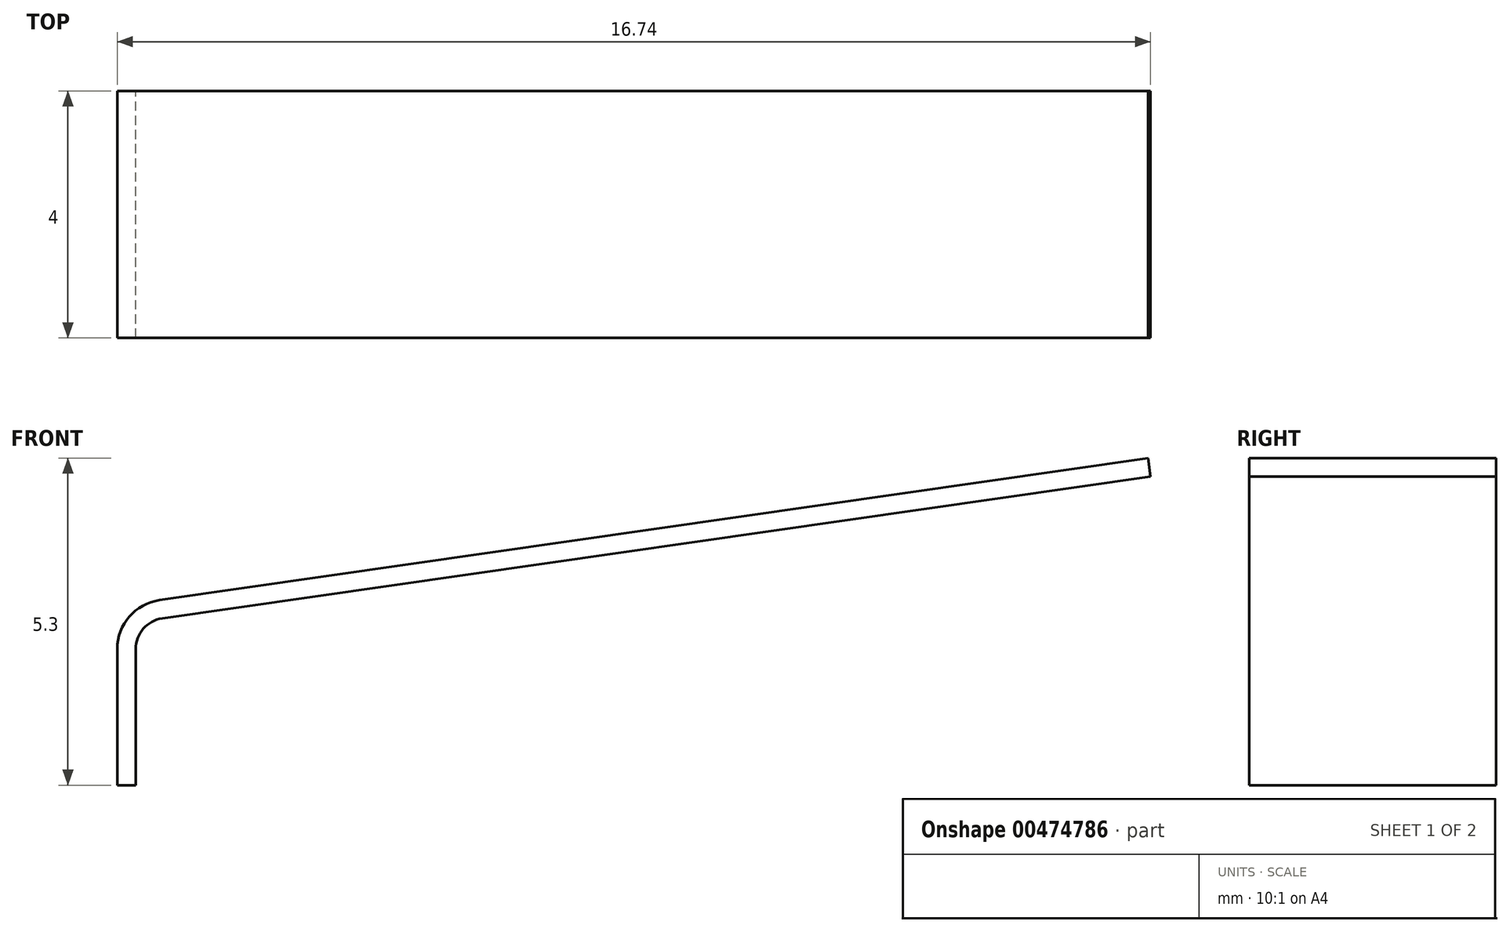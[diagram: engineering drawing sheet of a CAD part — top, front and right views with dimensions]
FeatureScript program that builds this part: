
annotation { "Feature Type Name" : "Feature", "Feature Type Description" : "" }
export const myFeature = defineFeature(function(context is Context, id is Id, definition is map)
    precondition{}
    {
        {
            var Q0;
            Q0=qCreatedBy(makeId("Front.planeOp"),FACE);
            var sketch = newSketch(context, id + "F0", { "sketchPlane" : qUnion([Q0])});
            skLineSegment(sketch, "E0", {"start": v(0, 0) * mm, "end": v(0, 2.2) * mm});
            skLineSegment(sketch, "E1", {"start": v(0.69, 3) * mm, "end": v(16.7, 5.3) * mm});
            skLineSegment(sketch, "E2", {"start": v(16.7, 5.3) * mm, "end": v(16.74, 5) * mm});
            skLineSegment(sketch, "E3", {"start": v(16.74, 5) * mm, "end": v(0.73, 2.7) * mm});
            skLineSegment(sketch, "E4", {"start": v(0.3, 2.2) * mm, "end": v(0.3, 0) * mm});
            skLineSegment(sketch, "E5", {"start": v(0.3, 0) * mm, "end": v(0, 0) * mm});
            skPoint(sketch, "E6.visualSharp", {"position": v(0.3, 2.64) * mm});
            skArc(sketch, "E6.filletArc", {"start": v(0.73, 2.7) * mm, "mid": v(0.42, 2.53) * mm, "end": v(0.3, 2.2) * mm});
            skPoint(sketch, "E7.visualSharp", {"position": v(0, 2.9) * mm});
            skArc(sketch, "E7.filletArc", {"start": v(0.69, 3) * mm, "mid": v(0.2, 2.73) * mm, "end": v(0, 2.2) * mm});
            skSolve(sketch);
        }
        {
            var Q0;
            Q0=qSketchRegion(id+"F0",true);
            extrude(context, id + "F1", {"entities" : qUnion([Q0]), "depth" : 4 * mm, "offsetDistance" : 25 * mm});
        }
    });
